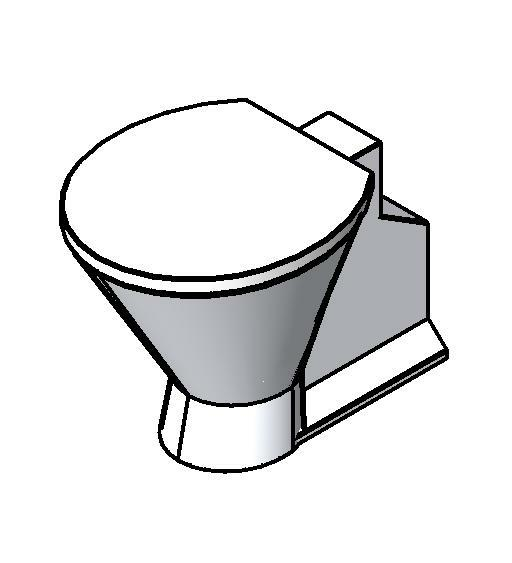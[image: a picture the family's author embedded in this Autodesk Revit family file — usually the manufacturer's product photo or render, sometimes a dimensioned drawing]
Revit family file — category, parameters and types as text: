
# Revit family: 23799-Deca_Acabamento Monocomando para Chuveiro Baixa e Alta Pressão Cromado_Gama_4993-13-CHU
name_source: partatom
category: Plumbing Fixtures
units: mm (PartAtom-declared; Revit-internal decimal feet)

## family parameters
Cut with Voids When Loaded = No
Host = Face
Part Type = Normal
Room Calculation Point = No
Round Connector Dimension = Use Radius
Shared = No

## types (1)
- 4993.C13.CHU_CROMADO
    Acompanha o Produto = Parafuso de fixação
    Aprovado por = quattroD
    Atendimento ao Cliente = 0800 011 7073
    CWFU = 0
    Categoria = METAIS PARA BANHEIRO
    Composição Anel Vedação = -
    Composição Assento = -
    Composição Básica = Liga de Cobre (bronze e latão),Liga de Zinco(zamac),Plásticos de Engenharia
    Composição Componente = -
    Consumo = -
    Cor Interna = -
    Cor Principal = Cromado
    Cor Secundária = -
    Cores Componente = -
    Criado por = quattroD
    Código Pai = 4993.C13.CHU
    Default Elevation = 1.1 m
    Description = ACABAMENTO MONOCOMANDO P/ CHUVEIRO BAIXA / ALTA PRESSAO GAMA- CROMADO
    Diâmetro Ponto de Esgoto = 0 m
    Diâmetro Água Fria = 0 m
    Informações Complementares = -
    Itens de Instalação = -
    Linha = Gama
    Manufacturer = Deca
    Material = Deca_Cromado
    Model = 4993.C13.CHU
    Norma = Não Possui
    Peso Líquido (Kg) = 0.305
    Pressão máx. funcionamento = -
    Pressão mín. Aquec. Acúmulo = -
    Pressão mín. Aquec. Passagem = -
    Pressão mín. funcionamento = -
    Raio Ponto de Esgoto = 0 m
    Raio Água Fria = 0 m
    Saída de Esgoto = -
    Segmento = -
    Tipo de dispositivo economizador = -
    Tipo de mecanismo utilizado = -
    Tipo de rosca de entrada = -
    Tipo de rosca de saída = -
    URL = www.deca.com.br
    Vazão na Pressão máx. (L/min) = -
    Vazão na Pressão mín. (L/min) = -
    WFU = 0

## geometry (parser evidence)
native form markers: Sweep x1
no freeform markers — native parametric forms only
